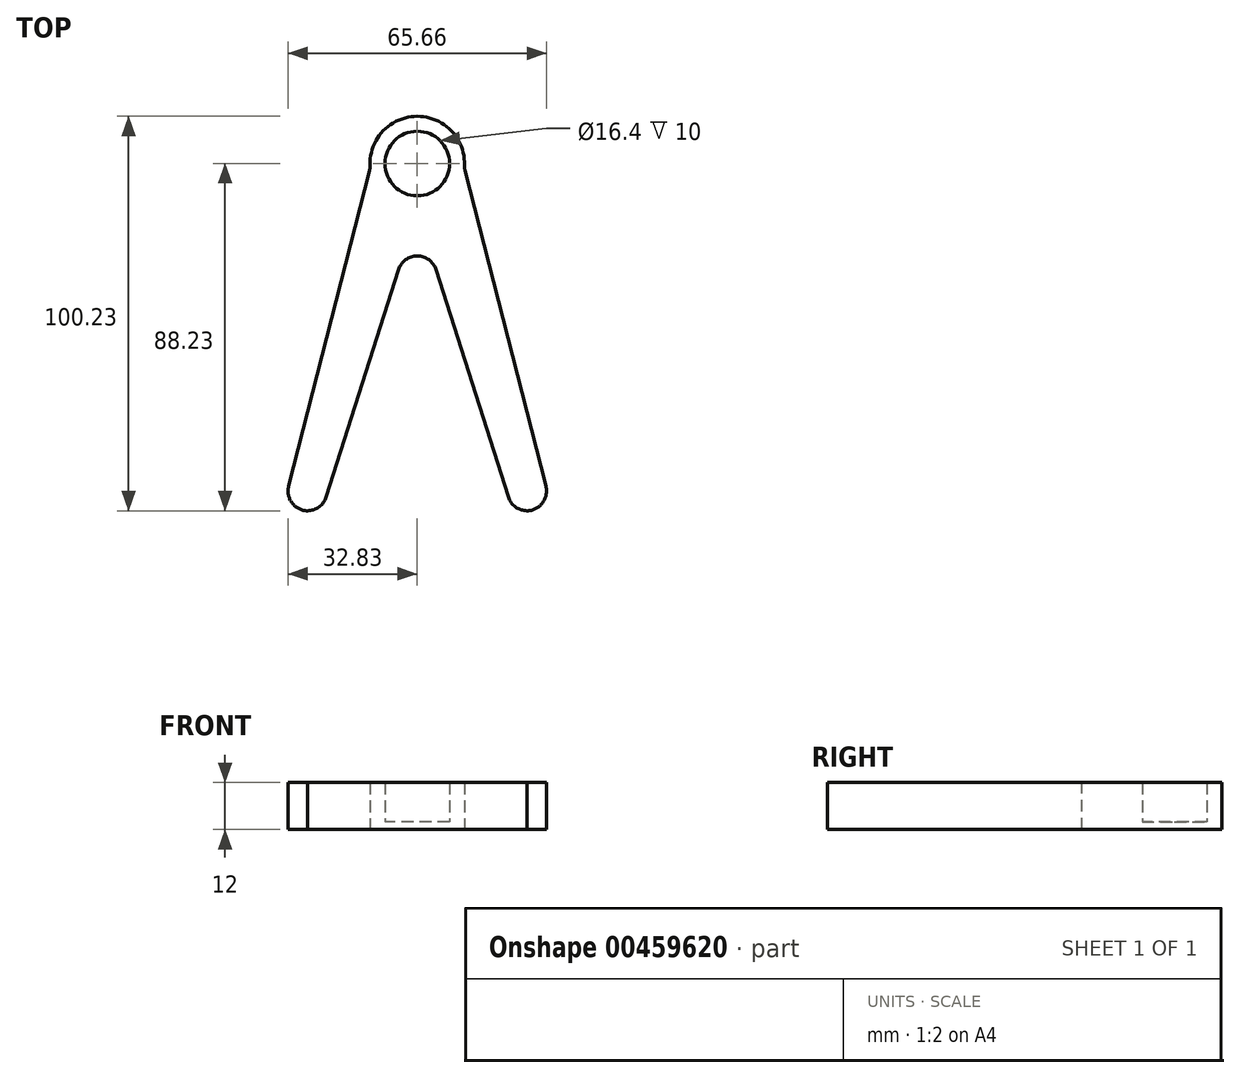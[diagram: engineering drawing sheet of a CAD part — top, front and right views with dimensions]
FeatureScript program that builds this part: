
annotation { "Feature Type Name" : "Feature", "Feature Type Description" : "" }
export const myFeature = defineFeature(function(context is Context, id is Id, definition is map)
    precondition{}
    {
        {
            var Q0;
            Q0=qCreatedBy(makeId("Top.planeOp"),FACE);
            var sketch = newSketch(context, id + "F0", { "sketchPlane" : qUnion([Q0])});
            skArc(sketch, "E0", {"start": v(11.95, 87.19) * mm, "mid": v(0, 100.23) * mm, "end": v(-11.95, 87.19) * mm});
            skCircle(sketch, "E1", {"center": v(0, 88.23) * mm, "radius": 8.2 * mm});
            skLineSegment(sketch, "E2", {"start": v(-11.95, 87.19) * mm, "end": v(11.95, 87.19) * mm, "construction": true});
            skLineSegment(sketch, "E3", {"start": v(-11.95, 87.19) * mm, "end": v(-34.27, 0) * mm});
            skLineSegment(sketch, "E4", {"start": v(-34.27, 0) * mm, "end": v(-24.27, 0) * mm});
            skLineSegment(sketch, "E5", {"start": v(-24.27, 0) * mm, "end": v(0, 76.23) * mm});
            skLineSegment(sketch, "E6", {"start": v(0, 76.23) * mm, "end": v(24.27, 0) * mm});
            skLineSegment(sketch, "E7", {"start": v(24.27, 0) * mm, "end": v(34.27, 0) * mm});
            skLineSegment(sketch, "E8", {"start": v(34.27, 0) * mm, "end": v(11.95, 87.19) * mm});
            skSolve(sketch);
        }
        {
            var Q0;
            Q0=makeQuery(id+"F0.imprint","IMPRINT",FACE,{"disambiguationData":[TD([[makeQuery(id+"F0.imprint","IMPRINT",EDGE,{"derivedFrom":sQuery(id+"F0.wireOp",EDGE,"E0")}),1.0]])]});
            extrude(context, id + "F1", {"entities" : qUnion([Q0]), "flatOperationType" : FlatOperationType.REMOVE, "offsetDistance" : 25 * mm, "depth" : 12 * mm, "domain" : OperationDomain.MODEL});
        }
        {
            var Q0;
            Q0=makeQuery(id+"F0.imprint","IMPRINT",FACE,{"disambiguationData":[TD([[makeQuery(id+"F0.imprint","IMPRINT",EDGE,{"derivedFrom":sQuery(id+"F0.wireOp",EDGE,"E1")}),1.0]])]});
            extrude(context, id + "F2", {"entities" : qUnion([Q0]), "operationType" : NewBodyOperationType.ADD, "flatOperationType" : FlatOperationType.REMOVE, "offsetDistance" : 25 * mm, "depth" : 2 * mm, "domain" : OperationDomain.MODEL});
        }
        {
            var Q0;
            Q0=makeQuery(id+"F1.opExtrude","SWEPT_EDGE",EDGE,{"disambiguationData":[OSD([sQuery(id+"F0.wireOp",EDGE,"E5"),sQuery(id+"F0.wireOp",EDGE,"E6")])]});
            var Q1;
            Q1=makeQuery(id+"F1.opExtrude","SWEPT_EDGE",EDGE,{"disambiguationData":[OSD([sQuery(id+"F0.wireOp",EDGE,"E4"),sQuery(id+"F0.wireOp",EDGE,"E5")])]});
            var Q2;
            Q2=makeQuery(id+"F1.opExtrude","SWEPT_EDGE",EDGE,{"disambiguationData":[OSD([sQuery(id+"F0.wireOp",EDGE,"E3"),sQuery(id+"F0.wireOp",EDGE,"E4")])]});
            var Q3;
            Q3=makeQuery(id+"F1.opExtrude","SWEPT_EDGE",EDGE,{"disambiguationData":[OSD([sQuery(id+"F0.wireOp",EDGE,"E6"),sQuery(id+"F0.wireOp",EDGE,"E7")])]});
            var Q4;
            Q4=makeQuery(id+"F1.opExtrude","SWEPT_EDGE",EDGE,{"disambiguationData":[OSD([sQuery(id+"F0.wireOp",EDGE,"E7"),sQuery(id+"F0.wireOp",EDGE,"E8")])]});
            var Q5;
            Q5=makeQuery(id+"F1.opExtrude","SWEPT_EDGE",EDGE,{"disambiguationData":[OSD([sQuery(id+"F0.wireOp",EDGE,"E0"),sQuery(id+"F0.wireOp",EDGE,"E8")])]});
            var Q6;
            Q6=makeQuery(id+"F1.opExtrude","SWEPT_EDGE",EDGE,{"disambiguationData":[OSD([sQuery(id+"F0.wireOp",EDGE,"E0"),sQuery(id+"F0.wireOp",EDGE,"E3")])]});
            fillet(context, id + "F3", {"entities" : qUnion([Q0, Q1, Q2, Q3, Q4, Q5, Q6]), "radius" : 5 * mm, "tangentPropagation" : true, "allowEdgeOverflow" : false});
        }
    });
